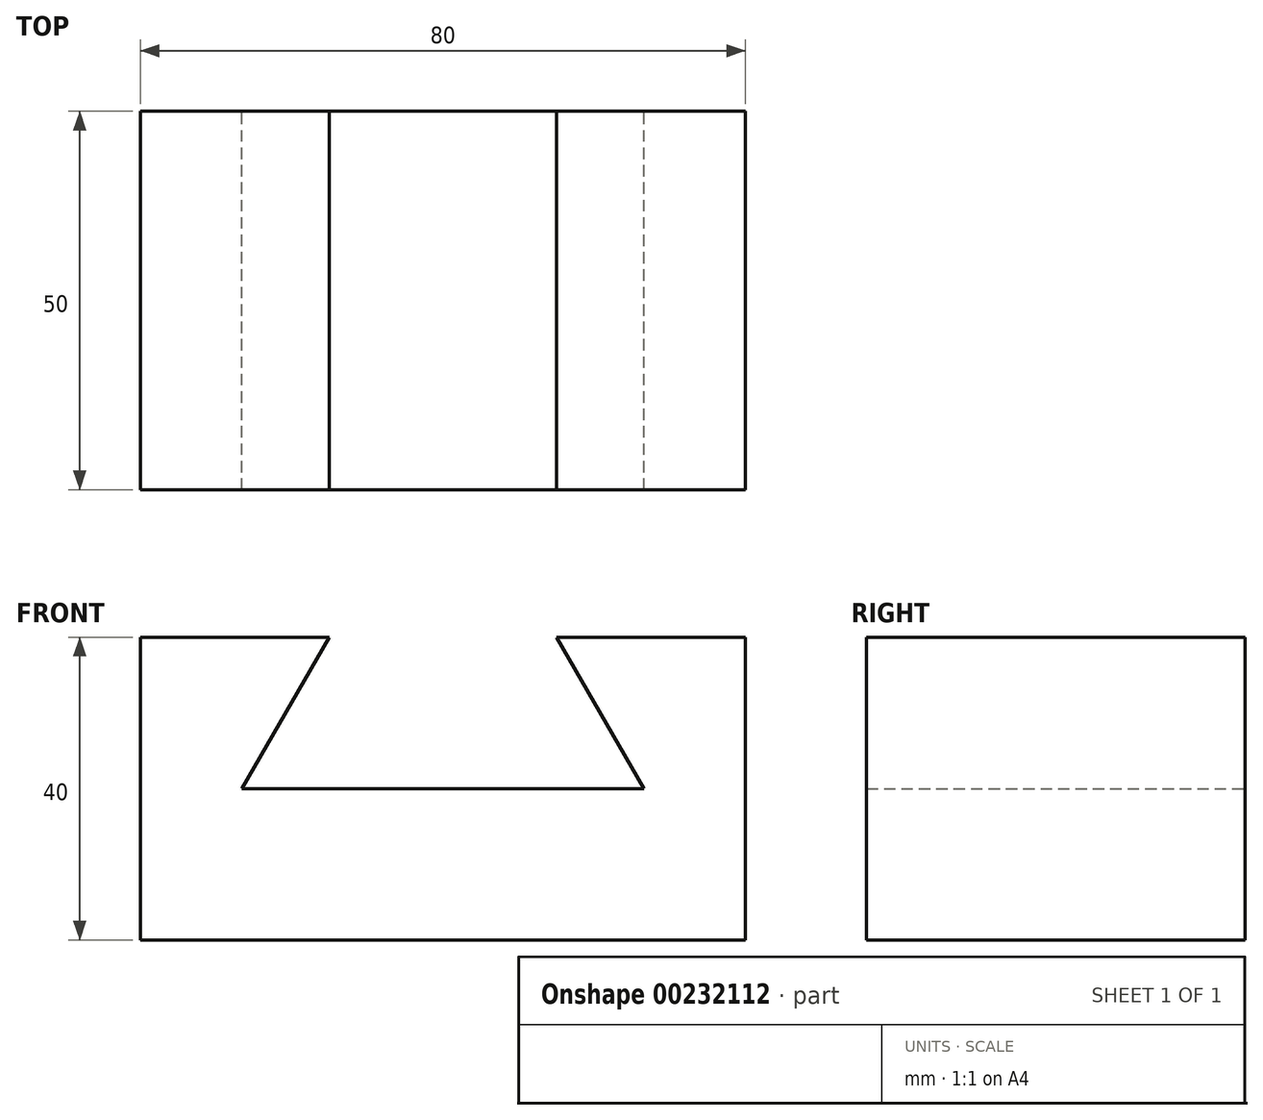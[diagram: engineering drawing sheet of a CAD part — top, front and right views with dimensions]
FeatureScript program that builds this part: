
annotation { "Feature Type Name" : "Feature", "Feature Type Description" : "" }
export const myFeature = defineFeature(function(context is Context, id is Id, definition is map)
    precondition{}
    {
        {
            var Q0;
            Q0=qCreatedBy(makeId("Front.planeOp"),FACE);
            var sketch = newSketch(context, id + "F0", { "sketchPlane" : qUnion([Q0])});
            skLineSegment(sketch, "E0.bottom", {"start": v(0, 0) * mm, "end": v(-80, 0) * mm});
            skLineSegment(sketch, "E0.top", {"start": v(0, 40) * mm, "end": v(-25, 40) * mm});
            skLineSegment(sketch, "E0.left", {"start": v(0, 0) * mm, "end": v(0, 40) * mm});
            skLineSegment(sketch, "E0.right", {"start": v(-80, 0) * mm, "end": v(-80, 40) * mm});
            skLineSegment(sketch, "E1", {"start": v(-40, 40) * mm, "end": v(-40, 0) * mm, "construction": true});
            skLineSegment(sketch, "E2", {"start": v(-55, 40) * mm, "end": v(-66.55, 20) * mm});
            skLineSegment(sketch, "E3", {"start": v(-66.55, 20) * mm, "end": v(-40, 20) * mm});
            skLineSegment(sketch, "E4.MirrorCS", {"start": v(-25, 40) * mm, "end": v(-13.45, 20) * mm});
            skLineSegment(sketch, "E5.MirrorCS", {"start": v(-13.45, 20) * mm, "end": v(-40, 20) * mm});
            skLineSegment(sketch, "E6.trimOffspring", {"start": v(-55, 40) * mm, "end": v(-80, 40) * mm});
            skSolve(sketch);
        }
        {
            var Q0;
            Q0=makeQuery(id+"F0.imprint","IMPRINT",FACE,{"disambiguationData":[TD([[makeQuery(id+"F0.imprint","IMPRINT",EDGE,{"derivedFrom":sQuery(id+"F0.wireOp",EDGE,"E0.bottom")}),-1.0]])]});
            extrude(context, id + "F1", {"entities" : qUnion([Q0]), "depth" : 50 * mm});
        }
    });
